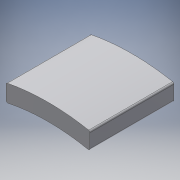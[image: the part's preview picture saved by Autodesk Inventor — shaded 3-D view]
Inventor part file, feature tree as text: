
AUTODESK INVENTOR PART (.ipt)
format: ipt  version: 2019.4 (Build 234330000, 330)  size: 109,568 bytes
history: native  units: mm
features: extrude x1, fillet x1, sketch x1
ambient origin geometry x8: Origin, YZ Plane, XZ Plane, XY Plane, X Axis, Y Axis, Z Axis, Center Point
bodies: Solid1 (feature_tree)
feature tree (3):
  extrude  "Extrusion1"  Depth=0.2mm
  fillet  "Fillet1"  Radius=10.0mm
  sketch  "Sketch1"  dims[d0=55.1mm d1=2.0mm d2=10.0mm d3=5.0mm d4=10.0mm d5=0.0mm d6=0.2mm]
